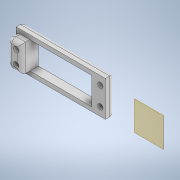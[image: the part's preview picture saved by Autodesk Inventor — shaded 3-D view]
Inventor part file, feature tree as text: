
AUTODESK INVENTOR PART (.ipt)
format: ipt  version: 2022 (Build 260153000, 153)  size: 233,472 bytes
history: native  units: in
note: dims shown in document units (in); Inventor stores cm internally (conversion verified against a paired STEP export)
features: sketch x6, extrude x5, projected_geometry x4, plane x2, fillet x2, mirror x1
ambient origin geometry x8: Origin, YZ Plane, XZ Plane, XY Plane, X Axis, Y Axis, Z Axis, Center Point
bodies: Solid1 (feature_tree)
feature tree (20):
  sketch  "Sketch1"  dims[d0=1.25in d1=3.937in]
  plane  "Work Plane1"
  sketch  "Sketch3"  dims[d3=0.25in d4=0.195in]
  plane  "Work Plane2"
  extrude  "Extrusion6"  Depth=3.937in
  extrude  "Extrusion7"  Depth=0.25in
  extrude  "Extrusion8"  Depth=0.157in
  extrude  "Extrusion9"  Depth=0.8in
  fillet  "Fillet4"  Radius=1.6in
  extrude  "Extrusion10"  Depth=0.315in
  mirror  "Mirror1"
  fillet  "Fillet7"  Radius=0.0787in
  projected_geometry  "Projected Loop2"
  sketch  "Sketch9"  dims[d5=0.157in d6=0.157in]
  sketch  "Sketch10"  dims[d7=0.195in d8=0.8in d9=1.6in]
  projected_geometry  "Projected Loop4"
  sketch  "Sketch12"  dims[d10=0.157in d11=0.315in d12=0.0787in]
  projected_geometry  "Projected Loop5"
  sketch  "Sketch14"  dims[d13=0.0787in d14=0.315in d15=0.118in d33=0.475in d34=0.25in d35=0.0in d38=0.157in d39=0.33in d40=0.157in d41=0.25in d42=0.0in d43=0.25in d44=0.0in d47=1.0in d48=0.0in d49=0.125in d54=0.1in d55=0.0in d56=0.125in]
  projected_geometry  "Projected Loop6"
